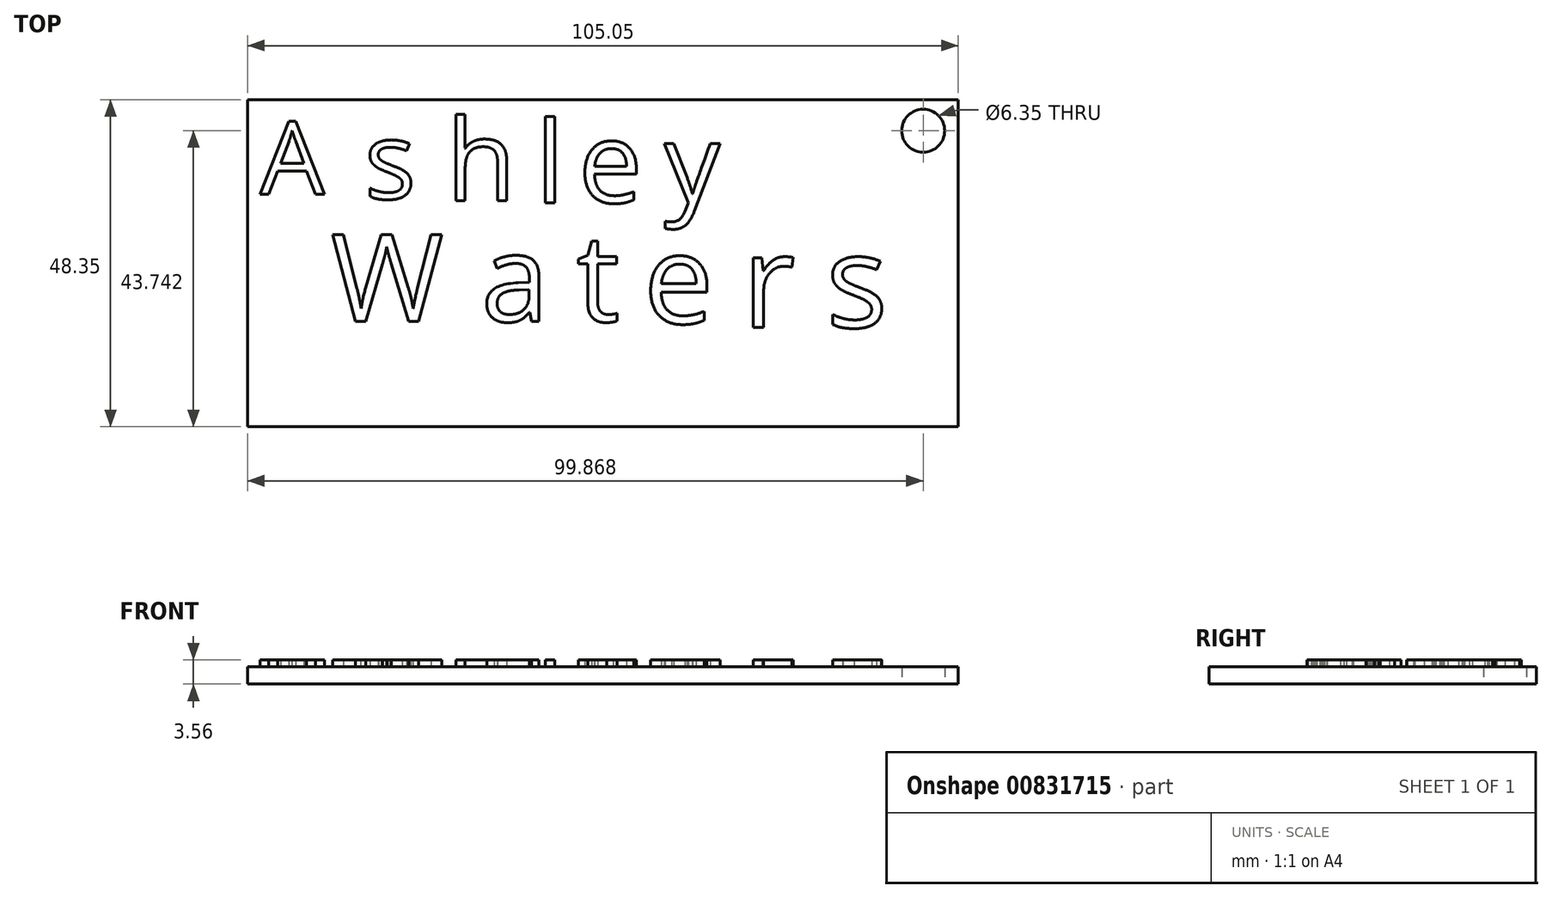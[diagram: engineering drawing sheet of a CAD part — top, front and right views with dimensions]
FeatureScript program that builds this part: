
annotation { "Feature Type Name" : "Feature", "Feature Type Description" : "" }
export const myFeature = defineFeature(function(context is Context, id is Id, definition is map)
    precondition{}
    {
        {
            var Q0;
            Q0=qCreatedBy(makeId("Top.planeOp"),FACE);
            var sketch = newSketch(context, id + "F0", { "sketchPlane" : qUnion([Q0])});
            skLineSegment(sketch, "E0.bottom", {"start": v(-51.66, 26.05) * mm, "end": v(53.39, 26.05) * mm});
            skLineSegment(sketch, "E0.top", {"start": v(-51.66, -22.3) * mm, "end": v(53.39, -22.3) * mm});
            skLineSegment(sketch, "E0.left", {"start": v(-51.66, 26.05) * mm, "end": v(-51.66, -22.3) * mm});
            skLineSegment(sketch, "E0.right", {"start": v(53.39, 26.05) * mm, "end": v(53.39, -22.3) * mm});
            skPoint(sketch, "E1", {"position": v(48.2, 21.44) * mm});
            skSolve(sketch);
        }
        {
            var Q0;
            Q0 = qSketchRegion(id + "F0", true);
            extrude(context, id + "F1", {"entities" : qUnion([Q0]), "depth" : 2.54 * mm, "offsetDistance" : 25.4 * mm});
        }
        {
            var Q0;
            Q0=makeQuery(id+"F1.opExtrude","CAP_FACE",FACE,{"disambiguationData":[OSD([sQuery(id+"F0.wireOp",EDGE,"E0.bottom"),sQuery(id+"F0.wireOp",EDGE,"E0.top"),sQuery(id+"F0.wireOp",EDGE,"E0.left"),sQuery(id+"F0.wireOp",EDGE,"E0.right")])],"isStart":false});
            var sketch = newSketch(context, id + "F2", { "sketchPlane" : qUnion([Q0])});
            skText(sketch, "E2", { "text": "A", "fontName": "OpenSans-Regular.ttf"});
            skText(sketch, "E3", { "text": "s", "fontName": "OpenSans-Regular.ttf"});
            skText(sketch, "E4", { "text": "h", "fontName": "OpenSans-Regular.ttf"});
            skText(sketch, "E5", { "text": "l\n", "fontName": "OpenSans-Regular.ttf"});
            skText(sketch, "E6", { "text": "e", "fontName": "OpenSans-Regular.ttf"});
            skText(sketch, "E7", { "text": "y", "fontName": "OpenSans-Regular.ttf"});
            skText(sketch, "E8", { "text": "W", "fontName": "OpenSans-Regular.ttf"});
            skText(sketch, "E9", { "text": "a", "fontName": "OpenSans-Regular.ttf"});
            skText(sketch, "E10", { "text": "t", "fontName": "OpenSans-Regular.ttf"});
            skText(sketch, "E11", { "text": "e", "fontName": "OpenSans-Regular.ttf"});
            skText(sketch, "E12", { "text": "r", "fontName": "OpenSans-Regular.ttf"});
            skText(sketch, "E13", { "text": "s", "fontName": "OpenSans-Regular.ttf"});
            const initialGuessF2  = {"E2": [-0.0498, 0.01208, 1, 0, 0.0108], "E3": [-0.0344, 0.01137, 1, 0, 0.01151], "E4": [-0.0223, 0.01108, 1, 0, 0.01209], "E5": [-0.00907, 0.0108, 1, 0, 0.01209], "E6": [-0.00273, 0.0108, 1, 0, 0.01209], "E7": [0.00993, 0.0108, 1, 0, 0.0118], "E8": [-0.03934, -0.00676, 1, 0, 0.01295], "E9": [-0.01712, -0.00676, 1, 0, 0.01295], "E10": [-0.00302, -0.00676, 1, 0, 0.01295], "E11": [0.0069, -0.00705, 1, 0, 0.01324], "E12": [0.02144, -0.00763, 1, 0, 0.01381], "E13": [0.03382, -0.00763, 1, 0, 0.01381]};
            skSetInitialGuess(sketch, initialGuessF2);
            skSolve(sketch);
        }
        {
            var Q0;
            Q0=sQuery(id+"F0.wireOp",VERTEX,"E1");
            var Q1;
            Q1=makeQuery(id+"F1.opExtrude","SWEPT_BODY",BODY,{"disambiguationData":[OSD([sQuery(id+"F0.wireOp",EDGE,"E0.bottom"),sQuery(id+"F0.wireOp",EDGE,"E0.top"),sQuery(id+"F0.wireOp",EDGE,"E0.left"),sQuery(id+"F0.wireOp",EDGE,"E0.right")])]});
            hole(context, id + "F3", {"style" : HoleStyle.SIMPLE, "endStyle" : HoleEndStyle.THROUGH, "oppositeDirection" : true, "holeDiameter" : 6.35 * mm, "majorDiameter" : 6.35 * mm, "isTappedThrough" : true, "tappedDepth" : 12.7 * mm, "tapClearance" : 3, "locations" : qUnion([Q0]), "scope" : qUnion([Q1])});
        }
        {
            var Q0;
            Q0 = qSketchRegion(id + "F2", true);
            extrude(context, id + "F4", {"entities" : qUnion([Q0]), "operationType" : NewBodyOperationType.ADD, "depth" : 1.02 * mm, "offsetDistance" : 25.4 * mm});
        }
    });
